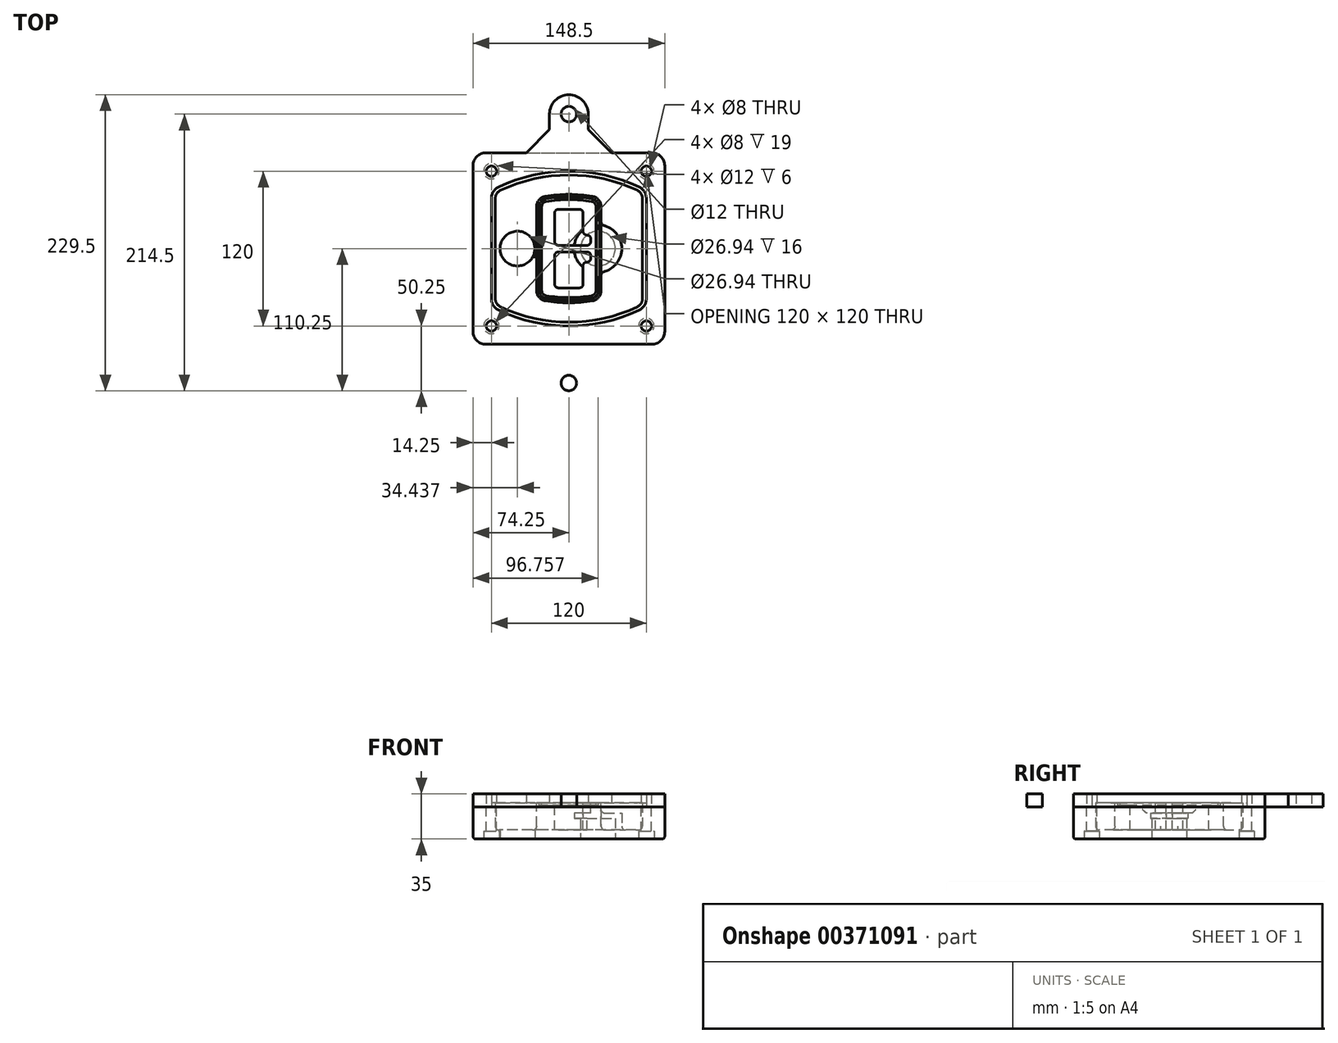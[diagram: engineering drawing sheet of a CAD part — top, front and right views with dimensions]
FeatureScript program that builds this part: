
annotation { "Feature Type Name" : "Feature", "Feature Type Description" : "" }
export const myFeature = defineFeature(function(context is Context, id is Id, definition is map)
    precondition{}
    {
        {
            var Q0;
            Q0=qCreatedBy(makeId("Top.planeOp"),FACE);
            var sketch = newSketch(context, id + "F0", { "sketchPlane" : qUnion([Q0])});
            skPoint(sketch, "E0.rect.middle", {"position": v(0, 0) * mm});
            skLineSegment(sketch, "E1.bottom", {"start": v(-64.25, -74.25) * mm, "end": v(64.25, -74.25) * mm});
            skLineSegment(sketch, "E1.top", {"start": v(-64.25, 74.25) * mm, "end": v(64.25, 74.25) * mm});
            skLineSegment(sketch, "E1.left", {"start": v(-74.25, -64.25) * mm, "end": v(-74.25, 64.25) * mm});
            skLineSegment(sketch, "E1.right", {"start": v(74.25, -64.25) * mm, "end": v(74.25, 64.25) * mm});
            skLineSegment(sketch, "E2", {"start": v(-74.25, 74.25) * mm, "end": v(74.25, -74.25) * mm, "construction": true});
            skLineSegment(sketch, "E3", {"start": v(74.25, 74.25) * mm, "end": v(-74.25, -74.25) * mm, "construction": true});
            skCircle(sketch, "E4", {"center": v(-60, 60) * mm, "radius": 4 * mm});
            skCircle(sketch, "E5", {"center": v(60, 60) * mm, "radius": 4 * mm});
            skCircle(sketch, "E6", {"center": v(60, -60) * mm, "radius": 4 * mm});
            skCircle(sketch, "E7", {"center": v(-60, -60) * mm, "radius": 4 * mm});
            skLineSegment(sketch, "E8", {"start": v(-60, 60) * mm, "end": v(60, 60) * mm, "construction": true});
            skLineSegment(sketch, "E9", {"start": v(60, 60) * mm, "end": v(60, -60) * mm, "construction": true});
            skLineSegment(sketch, "E10", {"start": v(60, -60) * mm, "end": v(-60, -60) * mm, "construction": true});
            skLineSegment(sketch, "E11", {"start": v(-60, -60) * mm, "end": v(-60, 60) * mm, "construction": true});
            skLineSegment(sketch, "E12", {"start": v(-60, 38.83) * mm, "end": v(-60, -38.83) * mm});
            skLineSegment(sketch, "E13", {"start": v(60, 38.83) * mm, "end": v(60, -38.83) * mm});
            skArc(sketch, "E14", {"start": v(54.26, 47.88) * mm, "mid": v(0, 60) * mm, "end": v(-54.26, 47.88) * mm});
            skArc(sketch, "E15", {"start": v(-54.26, -47.88) * mm, "mid": v(0, -60) * mm, "end": v(54.26, -47.88) * mm});
            skLineSegment(sketch, "E16", {"start": v(-60, 0) * mm, "end": v(60, 0) * mm, "construction": true});
            skPoint(sketch, "E17.visualSharp", {"position": v(-60, -45) * mm});
            skArc(sketch, "E17.filletArc", {"start": v(-60, -38.83) * mm, "mid": v(-58.44, -44.2) * mm, "end": v(-54.26, -47.88) * mm});
            skPoint(sketch, "E18.visualSharp", {"position": v(-60, 45) * mm});
            skArc(sketch, "E18.filletArc", {"start": v(-54.26, 47.88) * mm, "mid": v(-58.44, 44.2) * mm, "end": v(-60, 38.83) * mm});
            skPoint(sketch, "E19.visualSharp", {"position": v(60, 45) * mm});
            skArc(sketch, "E19.filletArc", {"start": v(60, 38.83) * mm, "mid": v(58.44, 44.2) * mm, "end": v(54.26, 47.88) * mm});
            skPoint(sketch, "E20.visualSharp", {"position": v(60, -45) * mm});
            skArc(sketch, "E20.filletArc", {"start": v(54.26, -47.88) * mm, "mid": v(58.44, -44.2) * mm, "end": v(60, -38.83) * mm});
            skPoint(sketch, "E21.visualSharp", {"position": v(-74.25, 74.25) * mm});
            skArc(sketch, "E21.filletArc", {"start": v(-64.25, 74.25) * mm, "mid": v(-71.32, 71.32) * mm, "end": v(-74.25, 64.25) * mm});
            skPoint(sketch, "E22.visualSharp", {"position": v(74.25, 74.25) * mm});
            skArc(sketch, "E22.filletArc", {"start": v(74.25, 64.25) * mm, "mid": v(71.32, 71.32) * mm, "end": v(64.25, 74.25) * mm});
            skPoint(sketch, "E23.visualSharp", {"position": v(74.25, -74.25) * mm});
            skArc(sketch, "E23.filletArc", {"start": v(64.25, -74.25) * mm, "mid": v(71.32, -71.32) * mm, "end": v(74.25, -64.25) * mm});
            skPoint(sketch, "E24.visualSharp", {"position": v(-74.25, -74.25) * mm});
            skArc(sketch, "E24.filletArc", {"start": v(-74.25, -64.25) * mm, "mid": v(-71.32, -71.32) * mm, "end": v(-64.25, -74.25) * mm});
            skArc(sketch, "E25.0", {"start": v(57, 38.83) * mm, "mid": v(55.9, 42.58) * mm, "end": v(52.98, 45.17) * mm});
            skLineSegment(sketch, "E25.1", {"start": v(57, 38.83) * mm, "end": v(57, -38.83) * mm});
            skArc(sketch, "E25.2", {"start": v(52.98, -45.17) * mm, "mid": v(55.9, -42.58) * mm, "end": v(57, -38.83) * mm});
            skArc(sketch, "E25.3", {"start": v(-52.98, -45.17) * mm, "mid": v(0, -57) * mm, "end": v(52.98, -45.17) * mm});
            skArc(sketch, "E25.4", {"start": v(-57, -38.83) * mm, "mid": v(-55.9, -42.58) * mm, "end": v(-52.98, -45.17) * mm});
            skArc(sketch, "E25.5", {"start": v(52.98, 45.17) * mm, "mid": v(0, 57) * mm, "end": v(-52.98, 45.17) * mm});
            skLineSegment(sketch, "E25.6", {"start": v(-57, 38.83) * mm, "end": v(-57, -38.83) * mm});
            skArc(sketch, "E25.7", {"start": v(-52.98, 45.17) * mm, "mid": v(-55.9, 42.58) * mm, "end": v(-57, 38.83) * mm});
            skArc(sketch, "E26.0", {"start": v(-55.96, 51.5) * mm, "mid": v(-61.82, 46.33) * mm, "end": v(-64, 38.83) * mm});
            skArc(sketch, "E26.1", {"start": v(55.96, 51.5) * mm, "mid": v(0, 64) * mm, "end": v(-55.96, 51.5) * mm});
            skArc(sketch, "E26.2", {"start": v(64, 38.83) * mm, "mid": v(61.82, 46.33) * mm, "end": v(55.96, 51.5) * mm});
            skLineSegment(sketch, "E26.3", {"start": v(64, 38.83) * mm, "end": v(64, -38.83) * mm});
            skArc(sketch, "E26.4", {"start": v(55.96, -51.5) * mm, "mid": v(61.82, -46.33) * mm, "end": v(64, -38.83) * mm});
            skLineSegment(sketch, "E26.5", {"start": v(-64, 38.83) * mm, "end": v(-64, -38.83) * mm});
            skArc(sketch, "E26.6", {"start": v(-55.96, -51.5) * mm, "mid": v(0, -64) * mm, "end": v(55.96, -51.5) * mm});
            skArc(sketch, "E26.7", {"start": v(-64, -38.83) * mm, "mid": v(-61.82, -46.33) * mm, "end": v(-55.96, -51.5) * mm});
            skSolve(sketch);
        }
        {
            var Q0;
            Q0=makeQuery(id+"F0.imprint","IMPRINT",FACE,{"disambiguationData":[TD([[makeQuery(id+"F0.imprint","IMPRINT",EDGE,{"derivedFrom":sQuery(id+"F0.wireOp",EDGE,"E1.bottom")}),1.0]])]});
            var Q1;
            Q1=makeQuery(id+"F0.imprint","IMPRINT",FACE,{"disambiguationData":[TD([[makeQuery(id+"F0.imprint","IMPRINT",EDGE,{"derivedFrom":sQuery(id+"F0.wireOp",EDGE,"E12")}),1.0]])]});
            var Q2;
            Q2=makeQuery(id+"F0.imprint","IMPRINT",FACE,{"disambiguationData":[TD([[makeQuery(id+"F0.imprint","IMPRINT",EDGE,{"derivedFrom":sQuery(id+"F0.wireOp",EDGE,"E25.0")}),1.0]])]});
            var Q3;
            Q3=makeQuery(id+"F0.imprint","IMPRINT",FACE,{"disambiguationData":[TD([[makeQuery(id+"F0.imprint","IMPRINT",EDGE,{"derivedFrom":sQuery(id+"F0.wireOp",EDGE,"E12")}),-1.0]])]});
            extrude(context, id + "F1", {"entities" : qUnion([Q0, Q1, Q2, Q3]), "oppositeDirection" : true, "depth" : 25 * mm});
        }
        {
            var Q0;
            Q0=makeQuery(id+"F0.imprint","IMPRINT",FACE,{"disambiguationData":[TD([[makeQuery(id+"F0.imprint","IMPRINT",EDGE,{"derivedFrom":sQuery(id+"F0.wireOp",EDGE,"E12")}),1.0]])]});
            extrude(context, id + "F2", {"entities" : qUnion([Q0]), "operationType" : NewBodyOperationType.ADD, "depth" : 3 * mm});
        }
        {
            var Q0;
            Q0=makeQuery(id+"F0.imprint","IMPRINT",FACE,{"disambiguationData":[TD([[makeQuery(id+"F0.imprint","IMPRINT",EDGE,{"derivedFrom":sQuery(id+"F0.wireOp",EDGE,"E25.0")}),1.0]])]});
            extrude(context, id + "F3", {"entities" : qUnion([Q0]), "operationType" : NewBodyOperationType.REMOVE, "oppositeDirection" : true, "depth" : 18 * mm});
        }
        {
            var Q0;
            Q0=makeQuery(id+"F2.opExtrude","CAP_FACE",FACE,{"disambiguationData":[OSD([sQuery(id+"F0.wireOp",EDGE,"E12"),sQuery(id+"F0.wireOp",EDGE,"E13"),sQuery(id+"F0.wireOp",EDGE,"E14"),sQuery(id+"F0.wireOp",EDGE,"E15"),sQuery(id+"F0.wireOp",EDGE,"E17.filletArc"),sQuery(id+"F0.wireOp",EDGE,"E18.filletArc"),sQuery(id+"F0.wireOp",EDGE,"E19.filletArc"),sQuery(id+"F0.wireOp",EDGE,"E20.filletArc"),sQuery(id+"F0.wireOp",EDGE,"E25.0"),sQuery(id+"F0.wireOp",EDGE,"E25.1"),sQuery(id+"F0.wireOp",EDGE,"E25.2"),sQuery(id+"F0.wireOp",EDGE,"E25.3"),sQuery(id+"F0.wireOp",EDGE,"E25.4"),sQuery(id+"F0.wireOp",EDGE,"E25.5"),sQuery(id+"F0.wireOp",EDGE,"E25.6"),sQuery(id+"F0.wireOp",EDGE,"E25.7")])],"isStart":false});
            var sketch = newSketch(context, id + "F4", { "sketchPlane" : qUnion([Q0])});
            skArc(sketch, "E27.0", {"start": v(-18.34, -40.45) * mm, "mid": v(0, -42) * mm, "end": v(18.34, -40.45) * mm});
            skArc(sketch, "E28.0", {"start": v(18.34, 40.45) * mm, "mid": v(0, 42) * mm, "end": v(-18.34, 40.45) * mm});
            skLineSegment(sketch, "E29", {"start": v(-25, 32.57) * mm, "end": v(-25, -32.57) * mm});
            skLineSegment(sketch, "E30", {"start": v(25, 32.57) * mm, "end": v(25, -32.57) * mm});
            skLineSegment(sketch, "E31", {"start": v(-25, 39.1) * mm, "end": v(25, 39.1) * mm, "construction": true});
            skLineSegment(sketch, "E32", {"start": v(-25, -39.1) * mm, "end": v(25, -39.1) * mm, "construction": true});
            skPoint(sketch, "E33.visualSharp", {"position": v(-25, 39.1) * mm});
            skArc(sketch, "E33.filletArc", {"start": v(-18.34, 40.45) * mm, "mid": v(-23.11, 37.73) * mm, "end": v(-25, 32.57) * mm});
            skPoint(sketch, "E34.visualSharp", {"position": v(25, 39.1) * mm});
            skArc(sketch, "E34.filletArc", {"start": v(25, 32.57) * mm, "mid": v(23.11, 37.73) * mm, "end": v(18.34, 40.45) * mm});
            skPoint(sketch, "E35.visualSharp", {"position": v(25, -39.1) * mm});
            skArc(sketch, "E35.filletArc", {"start": v(18.34, -40.45) * mm, "mid": v(23.11, -37.73) * mm, "end": v(25, -32.57) * mm});
            skPoint(sketch, "E36.visualSharp", {"position": v(-25, -39.1) * mm});
            skArc(sketch, "E36.filletArc", {"start": v(-25, -32.57) * mm, "mid": v(-23.11, -37.73) * mm, "end": v(-18.34, -40.45) * mm});
            skArc(sketch, "E37.0", {"start": v(52.98, 45.17) * mm, "mid": v(0, 57) * mm, "end": v(-52.98, 45.17) * mm});
            skArc(sketch, "E37.1", {"start": v(-52.98, 45.17) * mm, "mid": v(-55.9, 42.58) * mm, "end": v(-57, 38.83) * mm});
            skLineSegment(sketch, "E37.2", {"start": v(-57, 38.83) * mm, "end": v(-57, -38.83) * mm});
            skArc(sketch, "E37.3", {"start": v(-57, -38.83) * mm, "mid": v(-55.9, -42.58) * mm, "end": v(-52.98, -45.17) * mm});
            skArc(sketch, "E37.4", {"start": v(-52.98, -45.17) * mm, "mid": v(0, -57) * mm, "end": v(52.98, -45.17) * mm});
            skArc(sketch, "E37.5", {"start": v(52.98, -45.17) * mm, "mid": v(55.9, -42.58) * mm, "end": v(57, -38.83) * mm});
            skLineSegment(sketch, "E37.6", {"start": v(57, 38.83) * mm, "end": v(57, -38.83) * mm});
            skArc(sketch, "E37.7", {"start": v(57, 38.83) * mm, "mid": v(55.9, 42.58) * mm, "end": v(52.98, 45.17) * mm});
            skLineSegment(sketch, "E38.0", {"start": v(23, 32.57) * mm, "end": v(23, -32.57) * mm});
            skArc(sketch, "E38.1", {"start": v(18, -38.48) * mm, "mid": v(21.58, -36.44) * mm, "end": v(23, -32.57) * mm});
            skArc(sketch, "E38.2", {"start": v(-18, -38.48) * mm, "mid": v(0, -40) * mm, "end": v(18, -38.48) * mm});
            skArc(sketch, "E38.3", {"start": v(-23, -32.57) * mm, "mid": v(-21.58, -36.44) * mm, "end": v(-18, -38.48) * mm});
            skLineSegment(sketch, "E38.4", {"start": v(-23, 32.57) * mm, "end": v(-23, -32.57) * mm});
            skArc(sketch, "E38.5", {"start": v(23, 32.57) * mm, "mid": v(21.58, 36.44) * mm, "end": v(18, 38.48) * mm});
            skArc(sketch, "E38.6", {"start": v(-18, 38.48) * mm, "mid": v(-21.58, 36.44) * mm, "end": v(-23, 32.57) * mm});
            skArc(sketch, "E38.7", {"start": v(18, 38.48) * mm, "mid": v(0, 40) * mm, "end": v(-18, 38.48) * mm});
            skArc(sketch, "E39.0", {"start": v(21, 32.57) * mm, "mid": v(20.06, 35.15) * mm, "end": v(17.67, 36.5) * mm});
            skLineSegment(sketch, "E39.1", {"start": v(21, 32.57) * mm, "end": v(21, -32.57) * mm});
            skArc(sketch, "E39.2", {"start": v(17.67, -36.5) * mm, "mid": v(20.06, -35.15) * mm, "end": v(21, -32.57) * mm});
            skArc(sketch, "E39.3", {"start": v(-17.67, -36.5) * mm, "mid": v(0, -38) * mm, "end": v(17.67, -36.5) * mm});
            skArc(sketch, "E39.4", {"start": v(-21, -32.57) * mm, "mid": v(-20.06, -35.15) * mm, "end": v(-17.67, -36.5) * mm});
            skArc(sketch, "E39.5", {"start": v(17.67, 36.5) * mm, "mid": v(0, 38) * mm, "end": v(-17.67, 36.5) * mm});
            skLineSegment(sketch, "E39.6", {"start": v(-21, 32.57) * mm, "end": v(-21, -32.57) * mm});
            skArc(sketch, "E39.7", {"start": v(-17.67, 36.5) * mm, "mid": v(-20.06, 35.15) * mm, "end": v(-21, 32.57) * mm});
            skLineSegment(sketch, "E40", {"start": v(-25, 0) * mm, "end": v(25, 0) * mm, "construction": true});
            skLineSegment(sketch, "E41", {"start": v(-11, 5.5) * mm, "end": v(-11, 27.5) * mm});
            skLineSegment(sketch, "E42", {"start": v(-8, 30.5) * mm, "end": v(8, 30.5) * mm});
            skLineSegment(sketch, "E43", {"start": v(11, 27.5) * mm, "end": v(11, 13.5) * mm});
            skLineSegment(sketch, "E44", {"start": v(14, 10.5) * mm, "end": v(14, 10.5) * mm});
            skLineSegment(sketch, "E45", {"start": v(17, 7.5) * mm, "end": v(17, 5.5) * mm});
            skLineSegment(sketch, "E46", {"start": v(14, 2.5) * mm, "end": v(-8, 2.5) * mm});
            skPoint(sketch, "E47.visualSharp", {"position": v(-11, 30.5) * mm});
            skArc(sketch, "E47.filletArc", {"start": v(-8, 30.5) * mm, "mid": v(-10.12, 29.62) * mm, "end": v(-11, 27.5) * mm});
            skPoint(sketch, "E48.visualSharp", {"position": v(11, 30.5) * mm});
            skArc(sketch, "E48.filletArc", {"start": v(11, 27.5) * mm, "mid": v(10.12, 29.62) * mm, "end": v(8, 30.5) * mm});
            skPoint(sketch, "E49.visualSharp", {"position": v(11, 10.5) * mm});
            skArc(sketch, "E49.filletArc", {"start": v(11, 13.5) * mm, "mid": v(11.88, 11.38) * mm, "end": v(14, 10.5) * mm});
            skPoint(sketch, "E50.visualSharp", {"position": v(17, 10.5) * mm});
            skArc(sketch, "E50.filletArc", {"start": v(17, 7.5) * mm, "mid": v(16.12, 9.62) * mm, "end": v(14, 10.5) * mm});
            skPoint(sketch, "E51.visualSharp", {"position": v(17, 2.5) * mm});
            skArc(sketch, "E51.filletArc", {"start": v(14, 2.5) * mm, "mid": v(16.12, 3.38) * mm, "end": v(17, 5.5) * mm});
            skPoint(sketch, "E52.visualSharp", {"position": v(-11, 2.5) * mm});
            skArc(sketch, "E52.filletArc", {"start": v(-11, 5.5) * mm, "mid": v(-10.12, 3.38) * mm, "end": v(-8, 2.5) * mm});
            skLineSegment(sketch, "E53.0.MirrorCS", {"start": v(14, -2.5) * mm, "end": v(-8, -2.5) * mm});
            skArc(sketch, "E54.0.MirrorCS", {"start": v(-11, -5.5) * mm, "mid": v(-10.12, -3.38) * mm, "end": v(-8, -2.5) * mm});
            skLineSegment(sketch, "E55.0.MirrorCS", {"start": v(-11, -5.5) * mm, "end": v(-11, -27.5) * mm});
            skArc(sketch, "E56.0.MirrorCS", {"start": v(-8, -30.5) * mm, "mid": v(-10.12, -29.62) * mm, "end": v(-11, -27.5) * mm});
            skLineSegment(sketch, "E57.0.MirrorCS", {"start": v(-8, -30.5) * mm, "end": v(8, -30.5) * mm});
            skArc(sketch, "E58.0.MirrorCS", {"start": v(11, -27.5) * mm, "mid": v(10.12, -29.62) * mm, "end": v(8, -30.5) * mm});
            skLineSegment(sketch, "E59.0.MirrorCS", {"start": v(11, -27.5) * mm, "end": v(11, -13.5) * mm});
            skArc(sketch, "E60.0.MirrorCS", {"start": v(11, -13.5) * mm, "mid": v(11.88, -11.38) * mm, "end": v(14, -10.5) * mm});
            skArc(sketch, "E61.0.MirrorCS", {"start": v(17, -7.5) * mm, "mid": v(16.12, -9.62) * mm, "end": v(14, -10.5) * mm});
            skLineSegment(sketch, "E62.0.MirrorCS", {"start": v(17, -7.5) * mm, "end": v(17, -5.5) * mm});
            skArc(sketch, "E63.0.MirrorCS", {"start": v(14, -2.5) * mm, "mid": v(16.12, -3.38) * mm, "end": v(17, -5.5) * mm});
            skSolve(sketch);
        }
        {
            var Q0;
            Q0=makeQuery(id+"F4.imprint","IMPRINT",FACE,{"disambiguationData":[TD([[makeQuery(id+"F4.imprint","IMPRINT",EDGE,{"derivedFrom":sQuery(id+"F4.wireOp",EDGE,"E27.0")}),1.0]])]});
            var Q1;
            Q1=makeQuery(id+"F4.imprint","IMPRINT",FACE,{"disambiguationData":[TD([[makeQuery(id+"F4.imprint","IMPRINT",EDGE,{"derivedFrom":sQuery(id+"F4.wireOp",EDGE,"E38.0")}),-1.0]])]});
            var Q2;
            Q2=makeQuery(id+"F4.imprint","IMPRINT",FACE,{"disambiguationData":[TD([[makeQuery(id+"F4.imprint","IMPRINT",EDGE,{"derivedFrom":sQuery(id+"F4.wireOp",EDGE,"E39.0")}),1.0]])]});
            extrude(context, id + "F5", {"entities" : qUnion([Q0, Q1, Q2]), "operationType" : NewBodyOperationType.ADD, "endBound" : BoundingType.UP_TO_NEXT, "oppositeDirection" : true, "depth" : 25 * mm});
        }
        {
            var Q0;
            Q0=makeQuery(id+"F4.imprint","IMPRINT",FACE,{"disambiguationData":[TD([[makeQuery(id+"F4.imprint","IMPRINT",EDGE,{"derivedFrom":sQuery(id+"F4.wireOp",EDGE,"E38.0")}),-1.0]])]});
            extrude(context, id + "F6", {"entities" : qUnion([Q0]), "operationType" : NewBodyOperationType.REMOVE, "oppositeDirection" : true, "depth" : 2 * mm});
        }
        {
            var Q0;
            Q0=makeQuery(id+"F1.opExtrude","CAP_FACE",FACE,{"disambiguationData":[OSD([sQuery(id+"F0.wireOp",EDGE,"E1.bottom"),sQuery(id+"F0.wireOp",EDGE,"E1.top"),sQuery(id+"F0.wireOp",EDGE,"E1.left"),sQuery(id+"F0.wireOp",EDGE,"E1.right"),sQuery(id+"F0.wireOp",EDGE,"E4"),sQuery(id+"F0.wireOp",EDGE,"E5"),sQuery(id+"F0.wireOp",EDGE,"E6"),sQuery(id+"F0.wireOp",EDGE,"E7"),sQuery(id+"F0.wireOp",EDGE,"E21.filletArc"),sQuery(id+"F0.wireOp",EDGE,"E22.filletArc"),sQuery(id+"F0.wireOp",EDGE,"E23.filletArc"),sQuery(id+"F0.wireOp",EDGE,"E24.filletArc")])],"isStart":false});
            var sketch = newSketch(context, id + "F7", { "sketchPlane" : qUnion([Q0])});
            skCircle(sketch, "E64", {"center": v(22.5, 0) * mm, "radius": 13.47 * mm});
            skCircle(sketch, "E65", {"center": v(-39.81, 0) * mm, "radius": 13.47 * mm});
            skLineSegment(sketch, "E66", {"start": v(74.25, 0) * mm, "end": v(-74.25, 0) * mm});
            skCircle(sketch, "E67", {"center": v(22.5, 0) * mm, "radius": 18.47 * mm});
            skCircle(sketch, "E68", {"center": v(60, -60) * mm, "radius": 6 * mm});
            skCircle(sketch, "E69", {"center": v(-60, -60) * mm, "radius": 6 * mm});
            skCircle(sketch, "E70", {"center": v(-60, 60) * mm, "radius": 6 * mm});
            skCircle(sketch, "E71", {"center": v(60, 60) * mm, "radius": 6 * mm});
            skSolve(sketch);
        }
        {
            var Q0;
            {var subQ1=sQuery(id+"F7.wireOp",EDGE,"E66");var subQ4=sQuery(id+"F7.wireOp",EDGE,"E64");var subQ6=makeQuery(id+"F7.imprint","INTERSECT",VERTEX,{"disambiguationData":[OD(0.0)],"derivedFrom":[subQ4,subQ1]});Q0=makeQuery(id+"F7.imprint","IMPRINT",FACE,{"disambiguationData":[TD([[makeQuery(id+"F7.imprint","IMPRINT",EDGE,{"disambiguationData":[TD([[subQ6,-1.0]])],"derivedFrom":subQ4}),-1.0]])]});}
            var Q1;
            {var subQ0=sQuery(id+"F7.wireOp",EDGE,"E66");var subQ1=sQuery(id+"F7.wireOp",EDGE,"E64");var subQ3=makeQuery(id+"F7.imprint","INTERSECT",VERTEX,{"disambiguationData":[OD(0.0)],"derivedFrom":[subQ1,subQ0]});Q1=makeQuery(id+"F7.imprint","IMPRINT",FACE,{"disambiguationData":[TD([[makeQuery(id+"F7.imprint","IMPRINT",EDGE,{"disambiguationData":[TD([[subQ3,-1.0]])],"derivedFrom":subQ1}),1.0]])]});}
            var Q2;
            {var subQ0=sQuery(id+"F7.wireOp",EDGE,"E66");var subQ1=sQuery(id+"F7.wireOp",EDGE,"E64");var subQ3=makeQuery(id+"F7.imprint","INTERSECT",VERTEX,{"disambiguationData":[OD(0.0)],"derivedFrom":[subQ1,subQ0]});Q2=makeQuery(id+"F7.imprint","IMPRINT",FACE,{"disambiguationData":[TD([[makeQuery(id+"F7.imprint","IMPRINT",EDGE,{"disambiguationData":[TD([[subQ3,1.0]])],"derivedFrom":subQ1}),1.0]])]});}
            var Q3;
            {var subQ1=sQuery(id+"F7.wireOp",EDGE,"E66");var subQ4=sQuery(id+"F7.wireOp",EDGE,"E64");var subQ6=makeQuery(id+"F7.imprint","INTERSECT",VERTEX,{"disambiguationData":[OD(0.0)],"derivedFrom":[subQ4,subQ1]});Q3=makeQuery(id+"F7.imprint","IMPRINT",FACE,{"disambiguationData":[TD([[makeQuery(id+"F7.imprint","IMPRINT",EDGE,{"disambiguationData":[TD([[subQ6,1.0]])],"derivedFrom":subQ4}),-1.0]])]});}
            extrude(context, id + "F8", {"entities" : qUnion([Q0, Q1, Q2, Q3]), "operationType" : NewBodyOperationType.ADD, "oppositeDirection" : true, "depth" : 20 * mm});
        }
        {
            var Q0;
            {var subQ0=sQuery(id+"F7.wireOp",EDGE,"E66");var subQ1=sQuery(id+"F7.wireOp",EDGE,"E64");var subQ3=makeQuery(id+"F7.imprint","INTERSECT",VERTEX,{"disambiguationData":[OD(0.0)],"derivedFrom":[subQ1,subQ0]});Q0=makeQuery(id+"F7.imprint","IMPRINT",FACE,{"disambiguationData":[TD([[makeQuery(id+"F7.imprint","IMPRINT",EDGE,{"disambiguationData":[TD([[subQ3,-1.0]])],"derivedFrom":subQ1}),1.0]])]});}
            var Q1;
            {var subQ0=sQuery(id+"F7.wireOp",EDGE,"E66");var subQ1=sQuery(id+"F7.wireOp",EDGE,"E64");var subQ3=makeQuery(id+"F7.imprint","INTERSECT",VERTEX,{"disambiguationData":[OD(0.0)],"derivedFrom":[subQ1,subQ0]});Q1=makeQuery(id+"F7.imprint","IMPRINT",FACE,{"disambiguationData":[TD([[makeQuery(id+"F7.imprint","IMPRINT",EDGE,{"disambiguationData":[TD([[subQ3,1.0]])],"derivedFrom":subQ1}),1.0]])]});}
            extrude(context, id + "F9", {"entities" : qUnion([Q0, Q1]), "operationType" : NewBodyOperationType.REMOVE, "oppositeDirection" : true, "depth" : 16 * mm});
        }
        {
            var Q0;
            {var subQ0=sQuery(id+"F7.wireOp",EDGE,"E66");var subQ1=sQuery(id+"F7.wireOp",EDGE,"E65");var subQ3=makeQuery(id+"F7.imprint","INTERSECT",VERTEX,{"disambiguationData":[OD(0.0)],"derivedFrom":[subQ1,subQ0]});Q0=makeQuery(id+"F7.imprint","IMPRINT",FACE,{"disambiguationData":[TD([[makeQuery(id+"F7.imprint","IMPRINT",EDGE,{"disambiguationData":[TD([[subQ3,-1.0]])],"derivedFrom":subQ1}),1.0]])]});}
            var Q1;
            {var subQ0=sQuery(id+"F7.wireOp",EDGE,"E66");var subQ1=sQuery(id+"F7.wireOp",EDGE,"E65");var subQ3=makeQuery(id+"F7.imprint","INTERSECT",VERTEX,{"disambiguationData":[OD(0.0)],"derivedFrom":[subQ1,subQ0]});Q1=makeQuery(id+"F7.imprint","IMPRINT",FACE,{"disambiguationData":[TD([[makeQuery(id+"F7.imprint","IMPRINT",EDGE,{"disambiguationData":[TD([[subQ3,1.0]])],"derivedFrom":subQ1}),1.0]])]});}
            extrude(context, id + "F10", {"entities" : qUnion([Q0, Q1]), "operationType" : NewBodyOperationType.REMOVE, "oppositeDirection" : true, "depth" : 25 * mm});
        }
        {
            var Q0;
            Q0=makeQuery(id+"F7.imprint","IMPRINT",FACE,{"disambiguationData":[TD([[makeQuery(id+"F7.imprint","IMPRINT",EDGE,{"derivedFrom":sQuery(id+"F7.wireOp",EDGE,"E68")}),1.0]])]});
            var Q1;
            Q1=makeQuery(id+"F7.imprint","IMPRINT",FACE,{"disambiguationData":[TD([[makeQuery(id+"F7.imprint","IMPRINT",EDGE,{"derivedFrom":makeQuery(id+"F1.opExtrude","CAP_EDGE",EDGE,{"disambiguationData":[OSD([sQuery(id+"F0.wireOp",EDGE,"E5")])],"isStart":false})}),-1.0]])]});
            var Q2;
            Q2=makeQuery(id+"F7.imprint","IMPRINT",FACE,{"disambiguationData":[TD([[makeQuery(id+"F7.imprint","IMPRINT",EDGE,{"derivedFrom":sQuery(id+"F7.wireOp",EDGE,"E69")}),1.0]])]});
            var Q3;
            Q3=makeQuery(id+"F7.imprint","IMPRINT",FACE,{"disambiguationData":[TD([[makeQuery(id+"F7.imprint","IMPRINT",EDGE,{"derivedFrom":makeQuery(id+"F1.opExtrude","CAP_EDGE",EDGE,{"disambiguationData":[OSD([sQuery(id+"F0.wireOp",EDGE,"E4")])],"isStart":false})}),-1.0]])]});
            var Q4;
            Q4=makeQuery(id+"F7.imprint","IMPRINT",FACE,{"disambiguationData":[TD([[makeQuery(id+"F7.imprint","IMPRINT",EDGE,{"derivedFrom":sQuery(id+"F7.wireOp",EDGE,"E70")}),1.0]])]});
            var Q5;
            Q5=makeQuery(id+"F7.imprint","IMPRINT",FACE,{"disambiguationData":[TD([[makeQuery(id+"F7.imprint","IMPRINT",EDGE,{"derivedFrom":makeQuery(id+"F1.opExtrude","CAP_EDGE",EDGE,{"disambiguationData":[OSD([sQuery(id+"F0.wireOp",EDGE,"E7")])],"isStart":false})}),-1.0]])]});
            var Q6;
            Q6=makeQuery(id+"F7.imprint","IMPRINT",FACE,{"disambiguationData":[TD([[makeQuery(id+"F7.imprint","IMPRINT",EDGE,{"derivedFrom":sQuery(id+"F7.wireOp",EDGE,"E71")}),1.0]])]});
            var Q7;
            Q7=makeQuery(id+"F7.imprint","IMPRINT",FACE,{"disambiguationData":[TD([[makeQuery(id+"F7.imprint","IMPRINT",EDGE,{"derivedFrom":makeQuery(id+"F1.opExtrude","CAP_EDGE",EDGE,{"disambiguationData":[OSD([sQuery(id+"F0.wireOp",EDGE,"E6")])],"isStart":false})}),-1.0]])]});
            extrude(context, id + "F11", {"entities" : qUnion([Q0, Q1, Q2, Q3, Q4, Q5, Q6, Q7]), "operationType" : NewBodyOperationType.REMOVE, "oppositeDirection" : true, "depth" : 6 * mm});
        }
        {
            var Q0;
            Q0=makeQuery(id+"F9.boolean.opBoolean","COPY",FACE,{"derivedFrom":makeQuery(id+"F9.opExtrude","CAP_FACE",FACE,{"disambiguationData":[OSD([sQuery(id+"F7.wireOp",EDGE,"E64")])],"isStart":false})});
            var sketch = newSketch(context, id + "F12", { "sketchPlane" : qUnion([Q0])});
            skArc(sketch, "E72.0", {"start": v(11, 14.45) * mm, "mid": v(6.45, 9.13) * mm, "end": v(4.2, 2.5) * mm});
            skArc(sketch, "E72.1", {"start": v(4.2, -2.5) * mm, "mid": v(6.45, -9.13) * mm, "end": v(11, -14.45) * mm});
            skLineSegment(sketch, "E73", {"start": v(4.2, -2.5) * mm, "end": v(14, -2.5) * mm});
            skLineSegment(sketch, "E74.0", {"start": v(14, 2.5) * mm, "end": v(4.2, 2.5) * mm});
            skArc(sketch, "E74.1", {"start": v(14, 2.5) * mm, "mid": v(16.12, 3.38) * mm, "end": v(17, 5.5) * mm});
            skLineSegment(sketch, "E74.2", {"start": v(17, 7.5) * mm, "end": v(17, 5.5) * mm});
            skArc(sketch, "E74.3", {"start": v(17, 7.5) * mm, "mid": v(16.12, 9.62) * mm, "end": v(14, 10.5) * mm});
            skArc(sketch, "E74.4", {"start": v(11, 13.5) * mm, "mid": v(11.88, 11.38) * mm, "end": v(14, 10.5) * mm});
            skLineSegment(sketch, "E74.5", {"start": v(11, 14.45) * mm, "end": v(11, 13.5) * mm});
            skLineSegment(sketch, "E74.7", {"start": v(14, -2.5) * mm, "end": v(4.2, -2.5) * mm});
            skArc(sketch, "E74.8", {"start": v(14, -2.5) * mm, "mid": v(16.12, -3.38) * mm, "end": v(17, -5.5) * mm});
            skLineSegment(sketch, "E74.9", {"start": v(17, -7.5) * mm, "end": v(17, -5.5) * mm});
            skArc(sketch, "E74.10", {"start": v(17, -7.5) * mm, "mid": v(16.12, -9.62) * mm, "end": v(14, -10.5) * mm});
            skArc(sketch, "E74.11", {"start": v(11, -13.5) * mm, "mid": v(11.88, -11.38) * mm, "end": v(14, -10.5) * mm});
            skLineSegment(sketch, "E74.12", {"start": v(11, -14.45) * mm, "end": v(11, -13.5) * mm});
            skPoint(sketch, "E75.orphan", {"position": v(11, -27.5) * mm});
            skPoint(sketch, "E76.orphan", {"position": v(-8, -2.5) * mm});
            skPoint(sketch, "E77.orphan", {"position": v(-8, 2.5) * mm});
            skPoint(sketch, "E78.orphan", {"position": v(11, 27.5) * mm});
            skSolve(sketch);
        }
        {
            var Q0;
            {var subQ7=sQuery(id+"F12.wireOp",EDGE,"E72.0");var subQ14=sQuery(id+"F12.wireOp",EDGE,"E72.1");var subQ16=sQuery(id+"F12.wireOp",EDGE,"E74.1");var subQ18=sQuery(id+"F12.wireOp",EDGE,"E74.8");Q0=qUnion([makeQuery(id+"F12.imprint","IMPRINT",FACE,{"disambiguationData":[TD([[makeQuery(id+"F12.imprint","IMPRINT",EDGE,{"derivedFrom":subQ7}),1.0]])]}),makeQuery(id+"F12.imprint","IMPRINT",FACE,{"disambiguationData":[TD([[makeQuery(id+"F12.imprint","IMPRINT",EDGE,{"derivedFrom":subQ14}),1.0]])]}),makeQuery(id+"F12.imprint","IMPRINT",FACE,{"disambiguationData":[TD([[makeQuery(id+"F12.imprint","IMPRINT",EDGE,{"derivedFrom":subQ16}),1.0]])]}),makeQuery(id+"F12.imprint","IMPRINT",FACE,{"disambiguationData":[TD([[makeQuery(id+"F12.imprint","IMPRINT",EDGE,{"derivedFrom":subQ18}),-1.0]])]})]);}
            var Q1;
            Q1=makeQuery(id+"F5.boolean.opBoolean","SPLIT",FACE,{"disambiguationData":[TD([makeQuery(id+"F5.opExtrude","SWEPT_FACE",FACE,{"disambiguationData":[OSD([sQuery(id+"F4.wireOp",EDGE,"E41")])]})])],"derivedFrom":makeQuery(id+"F3.boolean.opBoolean","COPY",FACE,{"derivedFrom":makeQuery(id+"F3.opExtrude","CAP_FACE",FACE,{"disambiguationData":[OSD([sQuery(id+"F0.wireOp",EDGE,"E25.0"),sQuery(id+"F0.wireOp",EDGE,"E25.1"),sQuery(id+"F0.wireOp",EDGE,"E25.2"),sQuery(id+"F0.wireOp",EDGE,"E25.3"),sQuery(id+"F0.wireOp",EDGE,"E25.4"),sQuery(id+"F0.wireOp",EDGE,"E25.5"),sQuery(id+"F0.wireOp",EDGE,"E25.6"),sQuery(id+"F0.wireOp",EDGE,"E25.7")])],"isStart":false})})});
            extrude(context, id + "F13", {"entities" : qUnion([Q0]), "operationType" : NewBodyOperationType.REMOVE, "endBound" : BoundingType.UP_TO_SURFACE, "endBoundEntityFace" : qUnion([Q1]), "depth" : 25 * mm});
        }
        {
            var Q0;
            Q0=makeQuery(id+"F3.boolean.opBoolean","COPY",EDGE,{"derivedFrom":makeQuery(id+"F3.opExtrude","CAP_EDGE",EDGE,{"disambiguationData":[OSD([sQuery(id+"F0.wireOp",EDGE,"E25.6")])],"isStart":false})});
            var Q1;
            Q1=makeQuery(id+"F8.boolean.opBoolean","INTERSECT",EDGE,{"derivedFrom":[makeQuery(id+"F5.opExtrude","SWEPT_FACE",FACE,{"disambiguationData":[OSD([sQuery(id+"F4.wireOp",EDGE,"E30")])]}),makeQuery(id+"F8.opExtrude","CAP_FACE",FACE,{"disambiguationData":[OSD([sQuery(id+"F7.wireOp",EDGE,"E67")])],"isStart":false})]});
            var Q2;
            Q2=makeQuery(id+"F8.boolean.opBoolean","INTERSECT",EDGE,{"disambiguationData":[OD(1.0)],"derivedFrom":[makeQuery(id+"F5.opExtrude","SWEPT_FACE",FACE,{"disambiguationData":[OSD([sQuery(id+"F4.wireOp",EDGE,"E30")])]}),makeQuery(id+"F8.opExtrude","SWEPT_FACE",FACE,{"disambiguationData":[OSD([sQuery(id+"F7.wireOp",EDGE,"E67")])]})]});
            var Q3;
            {var subQ0=sQuery(id+"F4.wireOp",EDGE,"E30");Q3=makeQuery(id+"F8.boolean.opBoolean","SPLIT",EDGE,{"disambiguationData":[TD([makeQuery(id+"F5.opExtrude","SWEPT_FACE",FACE,{"disambiguationData":[OSD([sQuery(id+"F4.wireOp",EDGE,"E35.filletArc")])]})])],"derivedFrom":makeQuery(id+"F5.opExtrude","CAP_EDGE",EDGE,{"disambiguationData":[OSD([subQ0])],"isStart":false})});}
            var Q4;
            {var subQ0=sQuery(id+"F0.wireOp",EDGE,"E25.7");var subQ1=sQuery(id+"F0.wireOp",EDGE,"E25.1");var subQ2=sQuery(id+"F0.wireOp",EDGE,"E25.6");var subQ3=sQuery(id+"F0.wireOp",EDGE,"E25.5");var subQ4=sQuery(id+"F0.wireOp",EDGE,"E25.4");var subQ5=sQuery(id+"F0.wireOp",EDGE,"E25.0");var subQ6=sQuery(id+"F0.wireOp",EDGE,"E25.2");var subQ7=sQuery(id+"F0.wireOp",EDGE,"E25.3");Q4=makeQuery(id+"F8.boolean.opBoolean","INTERSECT",EDGE,{"derivedFrom":[makeQuery(id+"F5.boolean.opBoolean","SPLIT",FACE,{"disambiguationData":[TD([makeQuery(id+"F2.opExtrude","SWEPT_FACE",FACE,{"disambiguationData":[OSD([subQ5])]})])],"derivedFrom":makeQuery(id+"F3.boolean.opBoolean","COPY",FACE,{"derivedFrom":makeQuery(id+"F3.opExtrude","CAP_FACE",FACE,{"disambiguationData":[OSD([subQ5,subQ1,subQ6,subQ7,subQ4,subQ3,subQ2,subQ0])],"isStart":false})})}),makeQuery(id+"F8.opExtrude","SWEPT_FACE",FACE,{"disambiguationData":[OSD([sQuery(id+"F7.wireOp",EDGE,"E67")])]})]});}
            var Q5;
            Q5=makeQuery(id+"F8.boolean.opBoolean","INTERSECT",EDGE,{"disambiguationData":[OD(0.0)],"derivedFrom":[makeQuery(id+"F5.opExtrude","SWEPT_FACE",FACE,{"disambiguationData":[OSD([sQuery(id+"F4.wireOp",EDGE,"E30")])]}),makeQuery(id+"F8.opExtrude","SWEPT_FACE",FACE,{"disambiguationData":[OSD([sQuery(id+"F7.wireOp",EDGE,"E67")])]})]});
            fillet(context, id + "F14", {"entities" : qUnion([Q0, Q1, Q2, Q3, Q4, Q5]), "radius" : 3 * mm, "tangentPropagation" : true, "allowEdgeOverflow" : false});
        }
        {
            var Q0;
            Q0=makeQuery(id+"F1.opExtrude","CAP_EDGE",EDGE,{"disambiguationData":[OSD([sQuery(id+"F0.wireOp",EDGE,"E1.bottom")])],"isStart":false});
            fillet(context, id + "F15", {"entities" : qUnion([Q0]), "radius" : 2 * mm, "tangentPropagation" : true, "allowEdgeOverflow" : false});
        }
        {
            var Q0;
            {var subQ0=sQuery(id+"F0.wireOp",EDGE,"E21.filletArc");var subQ1=sQuery(id+"F0.wireOp",EDGE,"E7");var subQ2=sQuery(id+"F0.wireOp",EDGE,"E6");var subQ3=sQuery(id+"F0.wireOp",EDGE,"E5");var subQ4=sQuery(id+"F0.wireOp",EDGE,"E4");var subQ5=sQuery(id+"F0.wireOp",EDGE,"E22.filletArc");var subQ6=sQuery(id+"F0.wireOp",EDGE,"E1.bottom");var subQ7=sQuery(id+"F0.wireOp",EDGE,"E1.right");var subQ8=sQuery(id+"F0.wireOp",EDGE,"E1.top");var subQ9=sQuery(id+"F0.wireOp",EDGE,"E1.left");var subQ10=sQuery(id+"F0.wireOp",EDGE,"E23.filletArc");var subQ11=sQuery(id+"F0.wireOp",EDGE,"E24.filletArc");Q0=makeQuery(id+"F2.boolean.opBoolean","SPLIT",FACE,{"disambiguationData":[TD([makeQuery(id+"F1.opExtrude","SWEPT_FACE",FACE,{"disambiguationData":[OSD([subQ6])]})])],"derivedFrom":makeQuery(id+"F1.opExtrude","CAP_FACE",FACE,{"disambiguationData":[OSD([subQ6,subQ8,subQ9,subQ7,subQ4,subQ3,subQ2,subQ1,subQ0,subQ5,subQ10,subQ11])],"isStart":true})});}
            var sketch = newSketch(context, id + "F16", { "sketchPlane" : qUnion([Q0])});
            skPoint(sketch, "E79.centerSnap0", {"position": v(0, 74.25) * mm});
            skCircle(sketch, "E80", {"center": v(0, 104.25) * mm, "radius": 6 * mm});
            skArc(sketch, "E81", {"start": v(15, 104.25) * mm, "mid": v(0, 119.25) * mm, "end": v(-15, 104.25) * mm});
            skLineSegment(sketch, "E82", {"start": v(15, 104.25) * mm, "end": v(15, 92.25) * mm});
            skLineSegment(sketch, "E83", {"start": v(15, 92.25) * mm, "end": v(33, 74.25) * mm});
            skLineSegment(sketch, "E84", {"start": v(-15, 104.25) * mm, "end": v(-15, 92.25) * mm});
            skLineSegment(sketch, "E85", {"start": v(-15, 92.25) * mm, "end": v(-33, 74.25) * mm});
            skCircle(sketch, "E86.MirrorC", {"center": v(0, -104.25) * mm, "radius": 6 * mm});
            skLineSegment(sketch, "E87.MirrorCS", {"start": v(15, -92.25) * mm, "end": v(33, -74.25) * mm});
            skLineSegment(sketch, "E88.MirrorCS", {"start": v(-15, -104.25) * mm, "end": v(-15, -92.25) * mm});
            skLineSegment(sketch, "E89.MirrorCS", {"start": v(-15, -92.25) * mm, "end": v(-33, -74.25) * mm});
            skArc(sketch, "E90.MirrorCS", {"start": v(15, -104.25) * mm, "mid": v(0, -119.25) * mm, "end": v(-15, -104.25) * mm});
            skLineSegment(sketch, "E91.MirrorCS", {"start": v(15, -104.25) * mm, "end": v(15, -92.25) * mm});
            skSolve(sketch);
        }
        {
            var Q0;
            Q0=makeQuery(id+"F16.imprint","IMPRINT",FACE,{"disambiguationData":[TD([[makeQuery(id+"F16.imprint","IMPRINT",EDGE,{"derivedFrom":sQuery(id+"F16.wireOp",EDGE,"E80")}),-1.0]])]});
            var Q1;
            Q1=makeQuery(id+"F16.imprint","IMPRINT",FACE,{"disambiguationData":[TD([[makeQuery(id+"F16.imprint","IMPRINT",EDGE,{"derivedFrom":makeQuery(id+"F1.opExtrude","CAP_EDGE",EDGE,{"disambiguationData":[OSD([sQuery(id+"F0.wireOp",EDGE,"E1.left")])],"isStart":true})}),-1.0]])]});
            var Q2;
            Q2=makeQuery(id+"F16.imprint","IMPRINT",FACE,{"disambiguationData":[TD([[makeQuery(id+"F16.imprint","IMPRINT",EDGE,{"derivedFrom":sQuery(id+"F16.wireOp",EDGE,"E86.MirrorC")}),1.0]])]});
            extrude(context, id + "F17", {"entities" : qUnion([Q0, Q1, Q2]), "depth" : 10 * mm});
        }
    });
